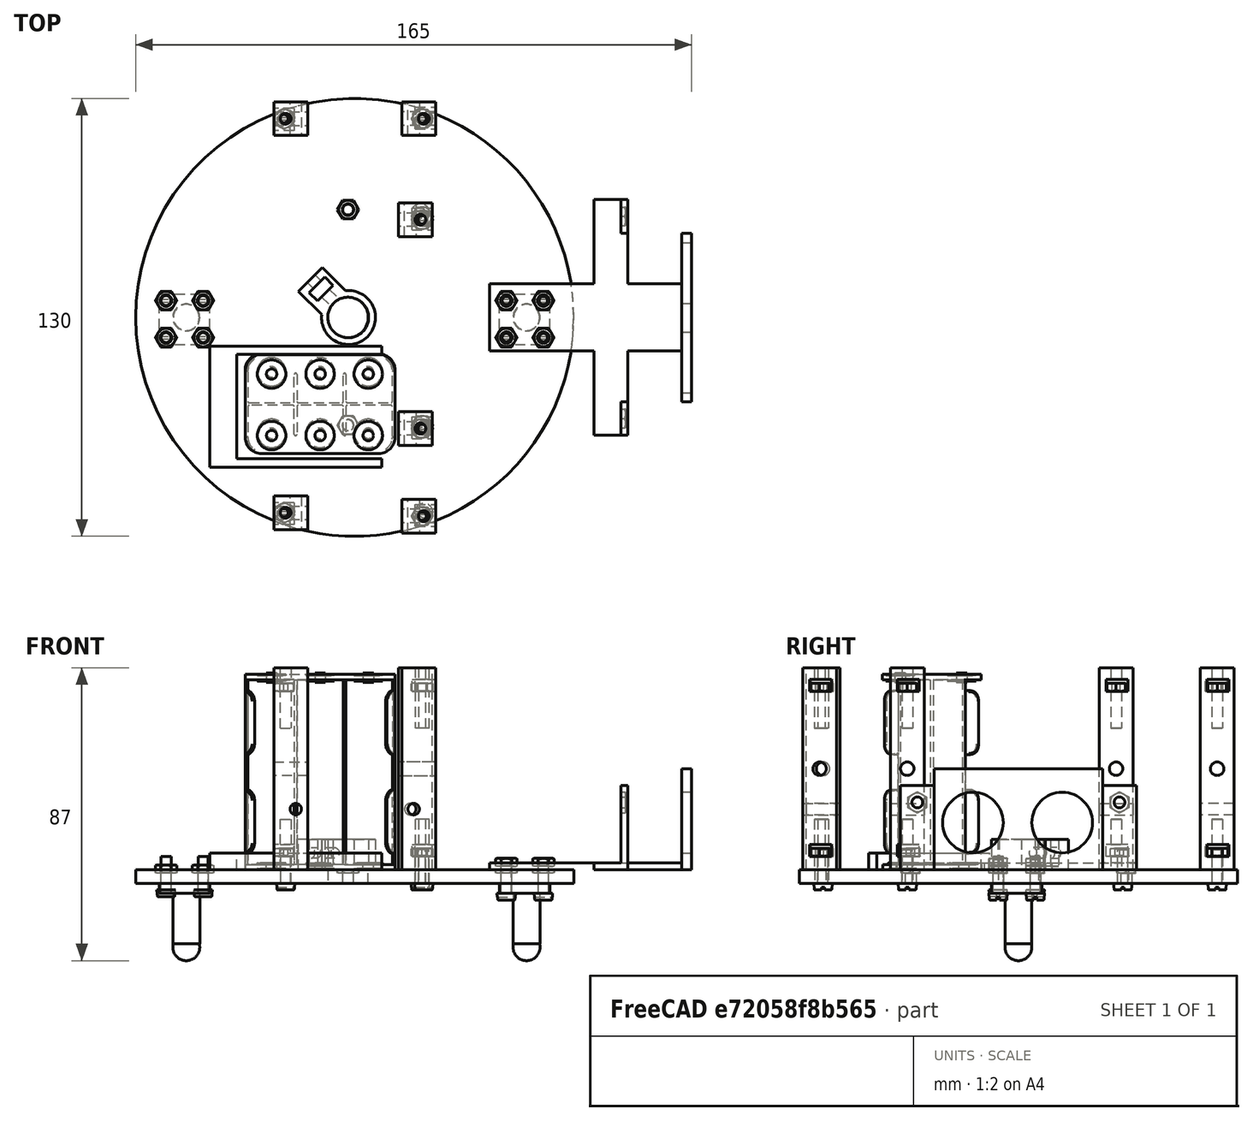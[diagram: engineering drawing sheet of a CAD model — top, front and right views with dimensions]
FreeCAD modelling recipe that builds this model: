
FCSTD DOCUMENT  (FreeCAD 0.21R33668 +26 (Git))
Label: ANIMACOLUMNAS
License: All rights reserved
LicenseURL: https://en.wikipedia.org/wiki/All_rights_reserved
objects: Part::FeaturePython×34, App::DocumentObjectGroupPython×13, Part::Feature×11, Part::MultiFuse×8
note: 53 computed .brp shape members not serialized (recipe doc carries the construction recipe); baked Part::Feature solids carry a one-line shape summary decoded from their .brp

FEATURE [Part::Feature] Cut009_solid  label="ballCSensor"
  Placement = pos=(0,0,20) rot=(0,0,1;0rad)
  shape: bbox 15 x 15 x 23 mm, 13 faces (baked)
FEATURE [Part::Feature] Fusion060_solid  label="plataformaInferior (Solid)"
  Placement = pos=(0,0,20) rot=(0,0,1;0rad)
  shape: bbox 130 x 130 x 13 mm, 195 faces (baked)
FEATURE [Part::FeaturePython] Nut  label="M3-Tuerca"  # Fasteners workbench fastener (typed FeaturePython)
  Placement = pos=(41,5,8) rot=(0,0,1;0rad)
  diameter = 4
  invert = false
  leftHanded = false
  matchOuter = false
  offset = 0
  thread = false
  type = 22
FEATURE [Part::FeaturePython] Nut001  label="M3-Tuerca004"  # Fasteners workbench fastener (typed FeaturePython)
  Placement = pos=(52,5,8) rot=(0,0,1;0rad)
  diameter = 4
  invert = false
  leftHanded = false
  matchOuter = false
  offset = 0
  thread = false
  type = 22
FEATURE [Part::FeaturePython] Nut002  label="M3-Tuerca006"  # Fasteners workbench fastener (typed FeaturePython)
  Placement = pos=(52,-6,8) rot=(0,0,1;0rad)
  diameter = 4
  invert = false
  leftHanded = false
  matchOuter = false
  offset = 0
  thread = false
  type = 22
FEATURE [Part::FeaturePython] Nut003  label="M3-Tuerca005"  # Fasteners workbench fastener (typed FeaturePython)
  Placement = pos=(41,-6,8) rot=(0,0,1;0rad)
  diameter = 4
  invert = false
  leftHanded = false
  matchOuter = false
  offset = 0
  thread = false
  type = 22
FEATURE [Part::MultiFuse] Fusion  label="tuercasBallCSensor"
  Placement = pos=(0,0,2) rot=(0,0,1;0rad)
  Shapes = -> [Nut,Nut001,Nut002,Nut003]
FEATURE [Part::FeaturePython] Nut004  label="M3-Tuerca007"  # Fasteners workbench fastener (typed FeaturePython)
  Placement = pos=(41,5,8) rot=(0,0,1;0rad)
  diameter = 4
  invert = false
  leftHanded = false
  matchOuter = false
  offset = 0
  thread = false
  type = 22
FEATURE [Part::FeaturePython] Nut005  label="M3-Tuerca008"  # Fasteners workbench fastener (typed FeaturePython)
  Placement = pos=(52,5,8) rot=(0,0,1;0rad)
  diameter = 4
  invert = false
  leftHanded = false
  matchOuter = false
  offset = 0
  thread = false
  type = 22
FEATURE [Part::FeaturePython] Nut006  label="M3-Tuerca009"  # Fasteners workbench fastener (typed FeaturePython)
  Placement = pos=(52,-6,8) rot=(0,0,1;0rad)
  diameter = 4
  invert = false
  leftHanded = false
  matchOuter = false
  offset = 0
  thread = false
  type = 22
FEATURE [Part::FeaturePython] Nut007  label="M3-Tuerca010"  # Fasteners workbench fastener (typed FeaturePython)
  Placement = pos=(41,-6,8) rot=(0,0,1;0rad)
  diameter = 4
  invert = false
  leftHanded = false
  matchOuter = false
  offset = 0
  thread = false
  type = 22
FEATURE [Part::MultiFuse] Fusion001  label="tuercasBallCLibre"
  Placement = pos=(-101,0,0) rot=(0,0,1;0rad)
  Shapes = -> [Nut004,Nut005,Nut006,Nut007]
FEATURE [Part::Feature] Cut009_solid001  label="ballCLibre"
  Placement = pos=(-101,0,20) rot=(0,0,1;0rad)
  shape: bbox 15 x 15 x 23 mm, 13 faces (baked)
FEATURE [Part::Feature] Cut_solid  label="soporteSensores (Solid)"
  Placement = pos=(15,0,20) rot=(0,0,1;0rad)
  shape: bbox 60 x 70 x 30 mm, 144 faces (baked)
FEATURE [Part::FeaturePython] Screw  label="M3x10-Tornillo"  # Fasteners workbench fastener (typed FeaturePython)
  Placement = pos=(-60,5,3) rot=(1,0,0;3.14159rad)
  diameter = 4
  invert = false
  leftHanded = false
  length = 4
  lengthCustom = 10
  matchOuter = false
  offset = 0
  thread = false
  type = 30
FEATURE [Part::FeaturePython] Screw001  label="M3x10-Tornillo001"  # Fasteners workbench fastener (typed FeaturePython)
  Placement = pos=(-60,-6,3) rot=(1,0,0;3.14159rad)
  diameter = 4
  invert = false
  leftHanded = false
  length = 4
  lengthCustom = 10
  matchOuter = false
  offset = 0
  thread = false
  type = 30
FEATURE [Part::FeaturePython] Screw002  label="M3x10-Tornillo002"  # Fasteners workbench fastener (typed FeaturePython)
  Placement = pos=(-49,-6,3) rot=(1,0,0;3.14159rad)
  diameter = 4
  invert = false
  leftHanded = false
  length = 4
  lengthCustom = 10
  matchOuter = false
  offset = 0
  thread = false
  type = 30
FEATURE [Part::FeaturePython] Screw003  label="M3x10-Tornillo003"  # Fasteners workbench fastener (typed FeaturePython)
  Placement = pos=(-49,5,3) rot=(1,0,0;3.14159rad)
  diameter = 4
  invert = false
  leftHanded = false
  length = 4
  lengthCustom = 10
  matchOuter = false
  offset = 0
  thread = false
  type = 30
FEATURE [Part::MultiFuse] Fusion002  label="tornillosBallClibre"
  Shapes = -> [Screw,Screw001,Screw002,Screw003]
FEATURE [Part::FeaturePython] Screw004  label="M3x10-Tornillo004"  # Fasteners workbench fastener (typed FeaturePython)
  Placement = pos=(-60,5,3) rot=(1,0,0;3.14159rad)
  diameter = 4
  invert = false
  leftHanded = false
  length = 4
  lengthCustom = 10
  matchOuter = false
  offset = 0
  thread = false
  type = 30
FEATURE [Part::FeaturePython] Screw005  label="M3x10-Tornillo005"  # Fasteners workbench fastener (typed FeaturePython)
  Placement = pos=(-60,-6,3) rot=(1,0,0;3.14159rad)
  diameter = 4
  invert = false
  leftHanded = false
  length = 4
  lengthCustom = 10
  matchOuter = false
  offset = 0
  thread = false
  type = 30
FEATURE [Part::FeaturePython] Screw006  label="M3x10-Tornillo006"  # Fasteners workbench fastener (typed FeaturePython)
  Placement = pos=(-49,-6,3) rot=(1,0,0;3.14159rad)
  diameter = 4
  invert = false
  leftHanded = false
  length = 4
  lengthCustom = 10
  matchOuter = false
  offset = 0
  thread = false
  type = 30
FEATURE [Part::FeaturePython] Screw007  label="M3x10-Tornillo007"  # Fasteners workbench fastener (typed FeaturePython)
  Placement = pos=(-49,5,3) rot=(1,0,0;3.14159rad)
  diameter = 4
  invert = false
  leftHanded = false
  length = 4
  lengthCustom = 10
  matchOuter = false
  offset = 0
  thread = false
  type = 30
FEATURE [Part::MultiFuse] Fusion003  label="tornillosBallCSensor"
  Placement = pos=(101,0,-1) rot=(0,0,1;0rad)
  Shapes = -> [Screw004,Screw005,Screw006,Screw007]
FEATURE [App::DocumentObjectGroupPython] SimpleGroup  # scripted group (container) (typed FeaturePython)
  AnimationStepTime = 0
  AnimationSteps = 20
  Distance = 19
  Revolutions = 0
  dir_vectors = (1) [(0,0,1)]
  rot_centers = (1) [(-54.5,-0.5,-14)]
  rot_vectors = (1) [(0,0,1)]
FEATURE [App::DocumentObjectGroupPython] SimpleGroup003  # scripted group (container) (typed FeaturePython)
  AnimationStepTime = 0
  AnimationSteps = 20
  Distance = 20
  Revolutions = 0
  dir_vectors = (1) [(0,0,-1)]
  rot_centers = (1) [(-60,-6,26)]
  rot_vectors = (1) [(0,0,-1)]
FEATURE [App::DocumentObjectGroupPython] SimpleGroup004  # scripted group (container) (typed FeaturePython)
  AnimationStepTime = 0
  AnimationSteps = 20
  Distance = 40
  Revolutions = 0
  dir_vectors = (1) [(0,1.22465e-16,1)]
  rot_centers = (1) [(-60,5,-27)]
  rot_vectors = (1) [(0,1.22465e-16,1)]
FEATURE [App::DocumentObjectGroupPython] SimpleGroup005  # scripted group (container) (typed FeaturePython)
  AnimationStepTime = 0
  AnimationSteps = 20
  Distance = 19
  Revolutions = 0
  dir_vectors = (1) [(0,0,1)]
  rot_centers = (1) [(46.5,-0.5,-14)]
  rot_vectors = (1) [(0,0,1)]
FEATURE [Part::Feature] Part__Feature  label="6 x AAA Holder"
  Placement = pos=(-100,212,67) rot=(0.57735,0.57735,-0.57735;2.0944rad)
  shape: bbox 45.01 x 29.59 x 58.41 mm, 300 faces, 8 solids (baked)
FEATURE [App::DocumentObjectGroupPython] SimpleGroup006  # scripted group (container) (typed FeaturePython)
  AnimationStepTime = 0
  AnimationSteps = 20
  Distance = 100
  Revolutions = 0
  dir_vectors = (1) [(-1,-6.69631e-16,-2.22045e-16)]
  rot_centers = (1) [(13.5,-25.9132,38.8088)]
  rot_vectors = (1) [(-1,-6.69631e-16,-2.22045e-16)]
FEATURE [App::DocumentObjectGroupPython] SimpleGroup007  # scripted group (container) (typed FeaturePython)
  AnimationStepTime = 0
  AnimationSteps = 20
  Distance = 15
  Revolutions = 0
  dir_vectors = (1) [(0,0,-1)]
  rot_centers = (1) [(72,-3.55271e-16,24)]
  rot_vectors = (1) [(0,0,-1)]
FEATURE [App::DocumentObjectGroupPython] SimpleGroup008  # scripted group (container) (typed FeaturePython)
  AnimationStepTime = 0
  AnimationSteps = 20
  Distance = 18
  Revolutions = 0
  dir_vectors = (1) [(0,0,-1)]
  rot_centers = (1) [(52,-6,28)]
  rot_vectors = (1) [(0,0,-1)]
FEATURE [App::DocumentObjectGroupPython] SimpleGroup009  # scripted group (container) (typed FeaturePython)
  AnimationStepTime = 0
  AnimationSteps = 20
  Distance = 39
  Revolutions = 0
  dir_vectors = (1) [(0,0,1)]
  rot_centers = (1) [(52,-6,-27)]
  rot_vectors = (1) [(0,0,1)]
FEATURE [Part::Feature] Cut_solid006  label="columna (Solid)004"
  Placement = pos=(0,-21,0) rot=(0,0,1;0rad)
  shape: bbox 10 x 10 x 60 mm, 24 faces (baked)
FEATURE [Part::Feature] Cut_solid004  label="columna (Solid)002"
  Placement = pos=(-8,21,0) rot=(0,0,1;3.14159rad)
  shape: bbox 10 x 10 x 60 mm, 24 faces (baked)
FEATURE [Part::Feature] Cut_solid007  label="columna (Solid)005"
  Placement = pos=(-8,-96,0) rot=(0,0,1;3.14159rad)
  shape: bbox 10 x 10 x 60 mm, 24 faces (baked)
FEATURE [Part::Feature] Cut_solid003  label="columna (Solid)001"
  Placement = pos=(-1,67,0) rot=(0,0,1;0rad)
  shape: bbox 10 x 10 x 60 mm, 24 faces (baked)
FEATURE [Part::Feature] Cut_solid005  label="columna (Solid)003"
  Placement = pos=(0,97,0) rot=(0,0,1;0rad)
  shape: bbox 10 x 10 x 60 mm, 24 faces (baked)
FEATURE [Part::FeaturePython] Screw008  label="M3x10-Tornillo008"  # Fasteners workbench fastener (typed FeaturePython)
  Placement = pos=(-24.5,-58,5) rot=(1,0,0;3.14159rad)
  diameter = 4
  invert = false
  leftHanded = false
  length = 4
  lengthCustom = 10
  matchOuter = false
  offset = 0
  thread = false
  type = 30
FEATURE [Part::FeaturePython] Screw009  label="M3x10-Tornillo009"  # Fasteners workbench fastener (typed FeaturePython)
  Placement = pos=(16.5,-58,5) rot=(1,0,0;3.14159rad)
  diameter = 4
  invert = false
  leftHanded = false
  length = 4
  lengthCustom = 10
  matchOuter = false
  offset = 0
  thread = false
  type = 30
FEATURE [Part::FeaturePython] Screw010  label="M3x10-Tornillo010"  # Fasteners workbench fastener (typed FeaturePython)
  Placement = pos=(15.5,-33,5) rot=(1,0,0;3.14159rad)
  diameter = 4
  invert = false
  leftHanded = false
  length = 4
  lengthCustom = 10
  matchOuter = false
  offset = 0
  thread = false
  type = 30
FEATURE [Part::FeaturePython] Screw011  label="M3x10-Tornillo011"  # Fasteners workbench fastener (typed FeaturePython)
  Placement = pos=(15.5,31,5) rot=(1,0,0;3.14159rad)
  diameter = 4
  invert = false
  leftHanded = false
  length = 4
  lengthCustom = 10
  matchOuter = false
  offset = 0
  thread = false
  type = 30
FEATURE [Part::FeaturePython] Screw012  label="M3x10-Tornillo012"  # Fasteners workbench fastener (typed FeaturePython)
  Placement = pos=(16.5,59,5) rot=(1,0,0;3.14159rad)
  diameter = 4
  invert = false
  leftHanded = false
  length = 4
  lengthCustom = 10
  matchOuter = false
  offset = 0
  thread = false
  type = 30
FEATURE [Part::FeaturePython] Screw013  label="M3x10-Tornillo013"  # Fasteners workbench fastener (typed FeaturePython)
  Placement = pos=(-24.5,59,5) rot=(1,0,0;3.14159rad)
  diameter = 4
  invert = false
  leftHanded = false
  length = 4
  lengthCustom = 10
  matchOuter = false
  offset = 0
  thread = false
  type = 30
FEATURE [Part::Feature] Cut_solid002  label="columna (Solid)"
  Placement = pos=(-1,5,0) rot=(0,0,1;0rad)
  shape: bbox 10 x 10 x 60 mm, 24 faces (baked)
FEATURE [Part::MultiFuse] Fusion004  label="columnas"
  Placement = pos=(0,0,20) rot=(0,0,1;0rad)
  Shapes = -> [Cut_solid006,Cut_solid004,Cut_solid007,Cut_solid003,Cut_solid005,Cut_solid002]
FEATURE [Part::MultiFuse] Fusion005  label="tornillosAbajo"
  Shapes = -> [Screw008,Screw009,Screw010,Screw011,Screw012,Screw013]
FEATURE [Part::FeaturePython] Nut008  label="M3-Tuerca011"  # Fasteners workbench fastener (typed FeaturePython)
  Placement = pos=(16,30,23) rot=(0,0,1;0rad)
  diameter = 4
  invert = false
  leftHanded = false
  matchOuter = false
  offset = 0
  thread = false
  type = 22
FEATURE [Part::FeaturePython] Nut009  label="M3-Tuerca012"  # Fasteners workbench fastener (typed FeaturePython)
  Placement = pos=(16,-32,23) rot=(0,0,1;0rad)
  diameter = 4
  invert = false
  leftHanded = false
  matchOuter = false
  offset = 0
  thread = false
  type = 22
FEATURE [Part::FeaturePython] Nut010  label="M3-Tuerca013"  # Fasteners workbench fastener (typed FeaturePython)
  Placement = pos=(16,-59,23) rot=(0,0,1;0rad)
  diameter = 4
  invert = false
  leftHanded = false
  matchOuter = false
  offset = 0
  thread = false
  type = 22
FEATURE [Part::FeaturePython] Nut011  label="M3-Tuerca014"  # Fasteners workbench fastener (typed FeaturePython)
  Placement = pos=(16,-59,72) rot=(0,0,1;0rad)
  diameter = 4
  invert = false
  leftHanded = false
  matchOuter = false
  offset = 0
  thread = false
  type = 22
FEATURE [Part::FeaturePython] Nut012  label="M3-Tuerca015"  # Fasteners workbench fastener (typed FeaturePython)
  Placement = pos=(16,-33,72) rot=(0,0,1;0rad)
  diameter = 4
  invert = false
  leftHanded = false
  matchOuter = false
  offset = 0
  thread = false
  type = 22
FEATURE [Part::FeaturePython] Nut013  label="M3-Tuerca016"  # Fasteners workbench fastener (typed FeaturePython)
  Placement = pos=(16,29,72) rot=(0,0,1;0rad)
  diameter = 4
  invert = false
  leftHanded = false
  matchOuter = false
  offset = 0
  thread = false
  type = 22
FEATURE [Part::FeaturePython] Nut014  label="M3-Tuerca017"  # Fasteners workbench fastener (typed FeaturePython)
  Placement = pos=(16,59,72) rot=(0,0,1;0rad)
  diameter = 4
  invert = false
  leftHanded = false
  matchOuter = false
  offset = 0
  thread = false
  type = 22
FEATURE [Part::FeaturePython] Nut015  label="M3-Tuerca018"  # Fasteners workbench fastener (typed FeaturePython)
  Placement = pos=(16,59,23) rot=(0,0,1;0.523599rad)
  diameter = 4
  invert = false
  leftHanded = false
  matchOuter = false
  offset = 0
  thread = false
  type = 22
FEATURE [Part::MultiFuse] Fusion006  label="tuercasDelante"
  Placement = pos=(0,0,-10) rot=(0,0,1;0rad)
  Shapes = -> [Nut015,Nut008,Nut009,Nut010,Nut011,Nut012,Nut013,Nut014]
FEATURE [App::DocumentObjectGroupPython] SimpleGroup010  # scripted group (container) (typed FeaturePython)
  AnimationStepTime = 0
  AnimationSteps = 20
  Distance = 20
  Revolutions = 0
  dir_vectors = (1) [(-1,5.55112e-16,0)]
  rot_centers = (1) [(38.25,59,24.2)]
  rot_vectors = (1) [(-1,5.55112e-16,0)]
FEATURE [Part::FeaturePython] Nut016  label="M3-Tuerca021"  # Fasteners workbench fastener (typed FeaturePython)
  Placement = pos=(-25,59,23) rot=(0,0,1;0.523599rad)
  diameter = 4
  invert = false
  leftHanded = false
  matchOuter = false
  offset = 0
  thread = false
  type = 22
FEATURE [Part::FeaturePython] Nut017  label="M3-Tuerca022"  # Fasteners workbench fastener (typed FeaturePython)
  Placement = pos=(-25,59,72) rot=(0,0,1;0.523599rad)
  diameter = 4
  invert = false
  leftHanded = false
  matchOuter = false
  offset = 0
  thread = false
  type = 22
FEATURE [Part::FeaturePython] Nut018  label="M3-Tuerca023"  # Fasteners workbench fastener (typed FeaturePython)
  Placement = pos=(-25,-58,72) rot=(0,0,1;0.523599rad)
  diameter = 4
  invert = false
  leftHanded = false
  matchOuter = false
  offset = 0
  thread = false
  type = 22
FEATURE [Part::FeaturePython] Nut019  label="M3-Tuerca024"  # Fasteners workbench fastener (typed FeaturePython)
  Placement = pos=(-25,-58,23) rot=(0,0,1;0.523599rad)
  diameter = 4
  invert = false
  leftHanded = false
  matchOuter = false
  offset = 0
  thread = false
  type = 22
FEATURE [Part::MultiFuse] Fusion007  label="tuercasAtras"
  Placement = pos=(0,0,-10) rot=(0,0,1;0rad)
  Shapes = -> [Nut019,Nut016,Nut017,Nut018]
FEATURE [App::DocumentObjectGroupPython] SimpleGroup011  # scripted group (container) (typed FeaturePython)
  AnimationStepTime = 0
  AnimationSteps = 20
  Distance = 20
  Revolutions = 0
  dir_vectors = (1) [(1,-1.66533e-16,0)]
  rot_centers = (1) [(-42.25,-58,73.2)]
  rot_vectors = (1) [(1,-1.66533e-16,0)]
FEATURE [App::DocumentObjectGroupPython] SimpleGroup012  # scripted group (container) (typed FeaturePython)
  AnimationStepTime = 0
  AnimationSteps = 20
  Distance = -10
  Revolutions = 0
  dir_vectors = (3) [(0,0,1),(0,0,1),(0,0,1)]
  rot_centers = (3) [(-2.75414,1.04693,9),(-2.75414,1.04693,9),(-2.75414,1.04693,9)]
  rot_vectors = (3) [(0,0,1),(0,0,1),(0,0,1)]
FEATURE [App::DocumentObjectGroupPython] SimpleGroup013  # scripted group (container) (typed FeaturePython)
  AnimationStepTime = 0
  AnimationSteps = 20
  Distance = -20
  Revolutions = 0
  dir_vectors = (1) [(0,0,-1)]
  rot_centers = (1) [(-4.00424,0.00296236,5)]
  rot_vectors = (1) [(0,0,-1)]
FEATURE [App::DocumentObjectGroupPython] ExplodedAssembly  # scripted group (container) (typed FeaturePython)
  AnimationStep = 0
  CurrentTrajectory = -1
  Group = -> [SimpleGroup,SimpleGroup003,SimpleGroup004,SimpleGroup005,SimpleGroup006,SimpleGroup007,SimpleGroup008,SimpleGroup009,SimpleGroup010,SimpleGroup011,SimpleGroup012,SimpleGroup013]
  InAnimation = false
  RemoveAllTrajectories = false
  ResetAnimation = false
